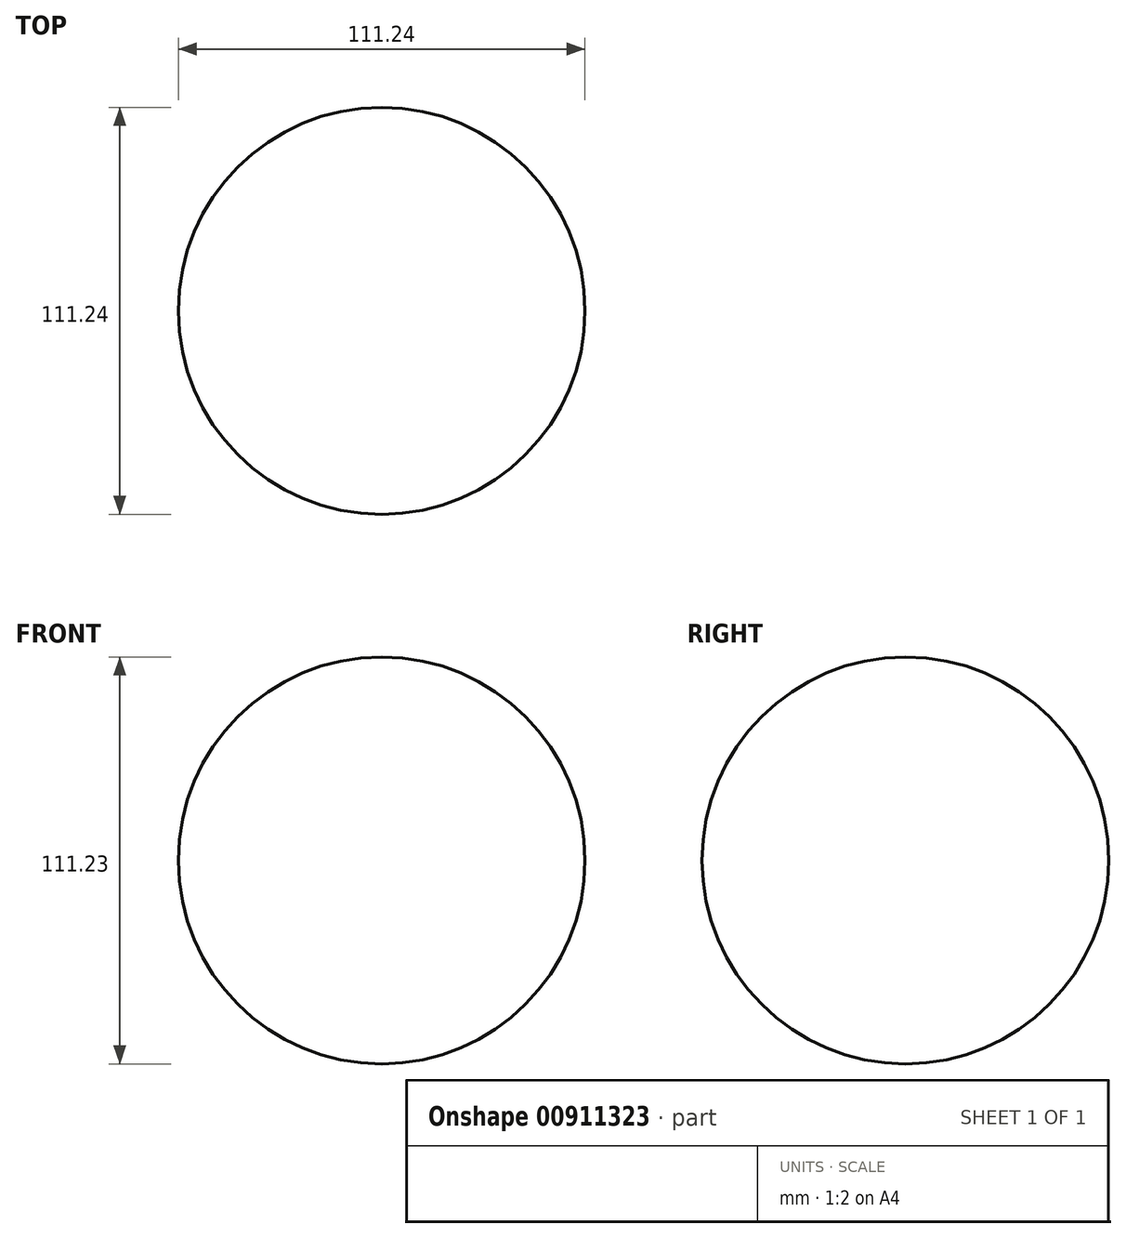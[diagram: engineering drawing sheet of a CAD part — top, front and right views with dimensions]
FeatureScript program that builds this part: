
annotation { "Feature Type Name" : "Feature", "Feature Type Description" : "" }
export const myFeature = defineFeature(function(context is Context, id is Id, definition is map)
    precondition{}
    {
        {
            var Q0;
            Q0=qCreatedBy(makeId("Front.planeOp"),FACE);
            var sketch = newSketch(context, id + "F0", { "sketchPlane" : qUnion([Q0])});
            skLineSegment(sketch, "E0.bottom", {"start": v(-63.93, 17.32) * mm, "end": v(47.3, 17.32) * mm});
            skLineSegment(sketch, "E0.top", {"start": v(-63.93, -41.8) * mm, "end": v(47.3, -41.8) * mm});
            skLineSegment(sketch, "E0.left", {"start": v(-63.93, 17.32) * mm, "end": v(-63.93, -41.8) * mm});
            skLineSegment(sketch, "E0.right", {"start": v(47.3, 17.32) * mm, "end": v(47.3, -41.8) * mm});
            skArc(sketch, "E1", {"start": v(47.3, 17.32) * mm, "mid": v(-8.3, 72.94) * mm, "end": v(-63.93, 17.32) * mm});
            skSolve(sketch);
        }
        {
            var Q0;
            Q0=makeQuery(id+"F0.imprint","IMPRINT",FACE,{"disambiguationData":[TD([[makeQuery(id+"F0.imprint","IMPRINT",EDGE,{"derivedFrom":sQuery(id+"F0.wireOp",EDGE,"E0.bottom")}),1.0]])]});
            var Q1;
            Q1=sQuery(id+"F0.wireOp",EDGE,"E0.bottom");
            revolve(context, id + "F1", {"surfaceOperationType" : NewSurfaceOperationType.NEW, "entities" : qUnion([Q0]), "axis" : qUnion([Q1]), "revolveType" : RevolveType.FULL});
        }
    });
